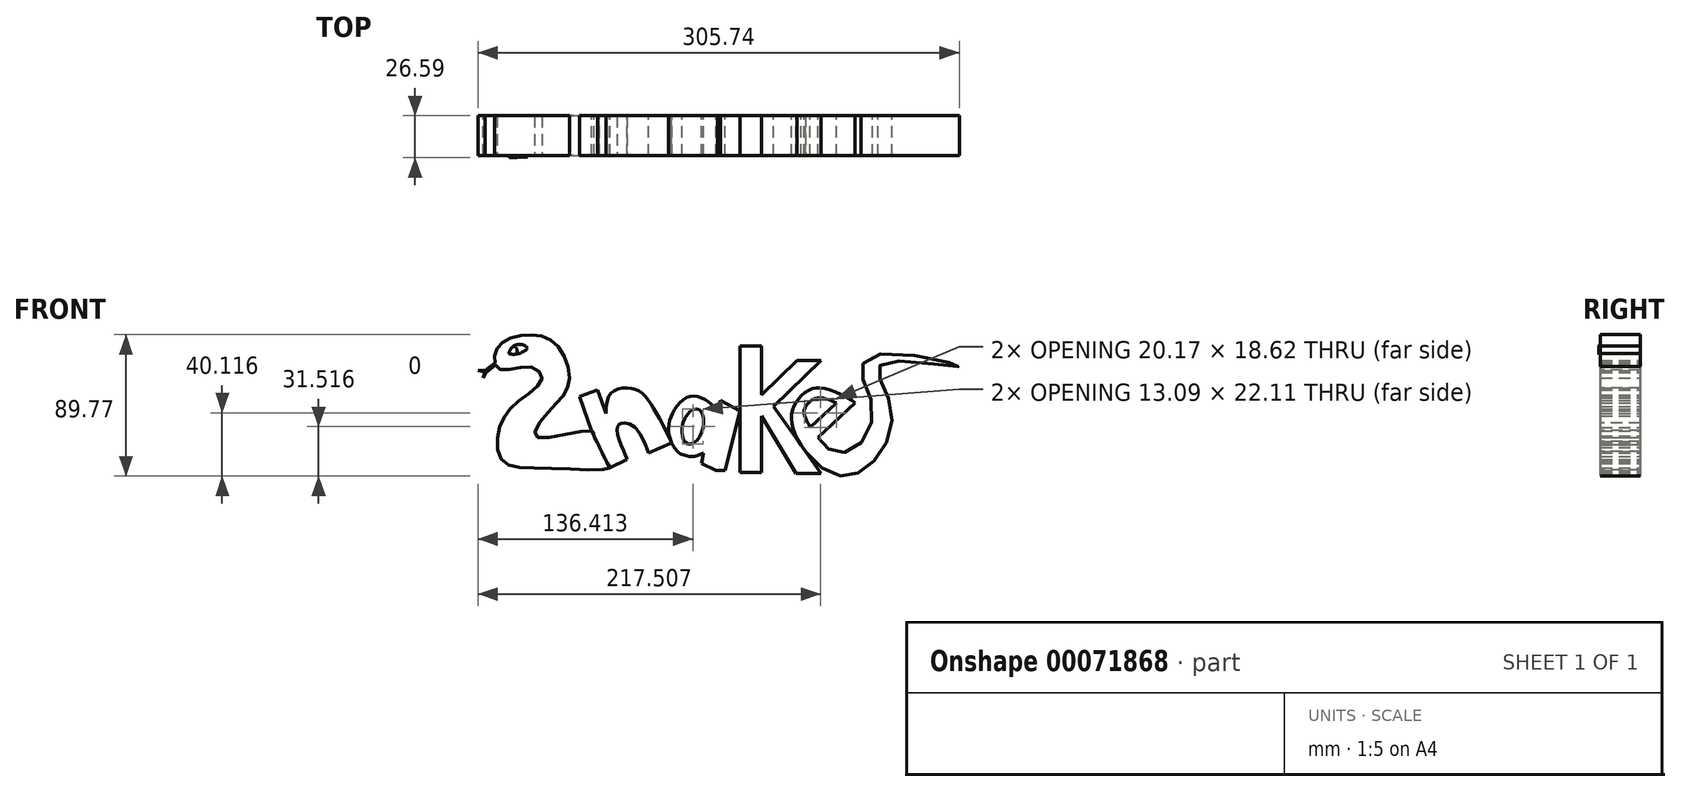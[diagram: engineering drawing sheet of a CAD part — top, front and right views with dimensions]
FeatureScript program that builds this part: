
annotation { "Feature Type Name" : "Feature", "Feature Type Description" : "" }
export const myFeature = defineFeature(function(context is Context, id is Id, definition is map)
    precondition{}
    {
        {
            var Q0;
            Q0=qCreatedBy(makeId("Front.planeOp"),FACE);
            var sketch = newSketch(context, id + "F0", { "sketchPlane" : qUnion([Q0])});
            skFitSpline(sketch, "E0", {"points": [v(-119.84, 21.1) * mm, v(-123.55, 27.84) * mm, v(-118.61, 38.3) * mm, v(-99.36, 43.22) * mm, v(-82.56, 35.03) * mm, v(-76.41, 12.09) * mm, v(-88.59, -4.8) * mm, v(-96.9, -21.5) * mm, v(-62.07, -17.82) * mm, v(-60.43, -21.12) * mm, v(-57.66, -26.68) * mm, v(-52.34, -37.36) * mm, v(-50.37, -41.31) * mm, v(-89.52, -41.59) * mm, v(-118.61, -36.67) * mm, v(-120.66, -16.6) * mm, v(-109.6, 0) * mm, v(-93.62, 14.95) * mm, v(-100.58, 22.74) * mm, v(-119.84, 21.1) * mm]});
            skLineSegment(sketch, "E1", {"start": v(-50.37, -41.31) * mm, "end": v(-62.07, -17.82) * mm});
            skLineSegment(sketch, "E2", {"start": v(-62.07, -17.82) * mm, "end": v(-69.7, 4.04) * mm});
            skLineSegment(sketch, "E3", {"start": v(-69.7, 4.04) * mm, "end": v(-58.05, 8.1) * mm});
            skLineSegment(sketch, "E4", {"start": v(-58.05, 8.1) * mm, "end": v(-52.9, -6.66) * mm});
            skFitSpline(sketch, "E5", {"points": [v(-52.9, -6.66) * mm, v(-49.31, 6.5) * mm, v(-35.25, 8.96) * mm, v(-24.7, 0) * mm, v(-11, -25.5) * mm], "startDerivative": vector(3.05, 68.8) * mm, "endDerivative": vector(42.91, -87.4) * mm});
            skLineSegment(sketch, "E6", {"start": v(-11, -25.5) * mm, "end": v(-25.76, -31.82) * mm});
            skFitSpline(sketch, "E7", {"points": [v(-25.76, -31.82) * mm, v(-32.79, -17.4) * mm, v(-40.17, -12.84) * mm, v(-45.8, -16) * mm, v(-39.47, -36.04) * mm, v(-39.82, -36.04) * mm], "startDerivative": vector(-23.2, 59.79) * mm, "endDerivative": vector(-11.8, 5.16) * mm});
            skLineSegment(sketch, "E8", {"start": v(-39.47, -36.04) * mm, "end": v(-50.37, -41.31) * mm});
            skLineSegment(sketch, "E9", {"start": v(-50.37, -41.31) * mm, "end": v(-50.37, -41.31) * mm});
            skLineSegment(sketch, "E10", {"start": v(7.83, -38.5) * mm, "end": v(17.12, -42.96) * mm});
            skLineSegment(sketch, "E11", {"start": v(17.12, -42.96) * mm, "end": v(22.69, -42.96) * mm});
            skLineSegment(sketch, "E12", {"start": v(22.69, -42.96) * mm, "end": v(32.34, -5.09) * mm});
            skLineSegment(sketch, "E13", {"start": v(32.34, -5.09) * mm, "end": v(20.08, 1.58) * mm});
            skLineSegment(sketch, "E14", {"start": v(20.08, 1.58) * mm, "end": v(18, -5) * mm});
            skLineSegment(sketch, "E15", {"start": v(7.83, -38.5) * mm, "end": v(9.16, -31.73) * mm});
            skFitSpline(sketch, "E16", {"points": [v(18, -5) * mm, v(11.8, 1.04) * mm, v(0.32, 4.05) * mm, v(-9.66, -5) * mm, v(-13.05, -16.28) * mm, v(-10.98, -25.69) * mm, v(-5.14, -32.46) * mm, v(4.08, -33.78) * mm, v(9.16, -31.73) * mm], "startDerivative": vector(-44.8, 53.4) * mm, "endDerivative": vector(47.88, 27.18) * mm});
            skEllipse(sketch, "E17", {"center": v(2.33, -14.96) * mm, "majorRadius": 11.45 * mm, "minorRadius": 6.5 * mm, "majorAxis": v(-0.26, -0.97)});
            skLineSegment(sketch, "E18", {"start": v(32.34, 36.08) * mm, "end": v(32.34, -44.27) * mm});
            skLineSegment(sketch, "E19", {"start": v(32.34, -44.27) * mm, "end": v(46.04, -44.27) * mm});
            skLineSegment(sketch, "E20", {"start": v(46.04, -44.27) * mm, "end": v(46.04, -8.22) * mm});
            skLineSegment(sketch, "E21", {"start": v(46.04, -8.22) * mm, "end": v(67.75, -44.67) * mm});
            skLineSegment(sketch, "E22", {"start": v(67.75, -44.67) * mm, "end": v(83.7, -44.67) * mm});
            skLineSegment(sketch, "E23", {"start": v(46.04, 5.07) * mm, "end": v(46.04, 36.08) * mm});
            skLineSegment(sketch, "E24", {"start": v(46.04, 36.08) * mm, "end": v(32.34, 36.08) * mm});
            skLineSegment(sketch, "E25", {"start": v(53.6, -2.23) * mm, "end": v(83.7, -44.67) * mm});
            skLineSegment(sketch, "E26", {"start": v(46.04, 5.07) * mm, "end": v(68.57, 26.83) * mm});
            skLineSegment(sketch, "E27", {"start": v(68.57, 26.83) * mm, "end": v(83.7, 26.83) * mm});
            skLineSegment(sketch, "E28", {"start": v(83.7, 26.83) * mm, "end": v(53.6, -2.23) * mm});
            skLineSegment(sketch, "E29", {"start": v(82, -21.92) * mm, "end": v(105.3, 0) * mm});
            skFitSpline(sketch, "E30", {"points": [v(105.3, 0) * mm, v(88.52, 8.55) * mm, v(77.48, 8.71) * mm, v(68.8, 1.6) * mm, v(65.03, -8.4) * mm, v(69.87, -24.91) * mm, v(90, -44.67) * mm, v(107.59, -44.16) * mm, v(124.35, -26.93) * mm, v(127.58, 0) * mm, v(119.85, 20.21) * mm, v(130, 26.5) * mm, v(171.65, 23.1) * mm, v(126.5, 31.4) * mm, v(109.22, 21.35) * mm, v(115.98, 0) * mm, v(108.58, -26.1) * mm, v(91.54, -30.93) * mm, v(82, -21.92) * mm], "startDerivative": vector(-184.22, 175.25) * mm, "endDerivative": vector(-182.9, 208.9) * mm});
            skFitSpline(sketch, "E31", {"points": [v(76.86, -15.67) * mm, v(73, -5.87) * mm, v(82, 3.14) * mm, v(93.51, 0) * mm], "startDerivative": vector(-2.6, 15.99) * mm, "endDerivative": vector(18.2, -6.44) * mm});
            skLineSegment(sketch, "E32", {"start": v(76.86, -15.67) * mm, "end": v(93.51, 0) * mm});
            skLineSegment(sketch, "E33", {"start": v(-123.28, 25.21) * mm, "end": v(-129.47, 20.44) * mm});
            skLineSegment(sketch, "E34", {"start": v(-129.47, 20.44) * mm, "end": v(-134.08, 20.44) * mm});
            skLineSegment(sketch, "E35", {"start": v(-134.08, 20.44) * mm, "end": v(-129.42, 19.73) * mm});
            skLineSegment(sketch, "E36", {"start": v(-129.42, 19.73) * mm, "end": v(-130.87, 15.73) * mm});
            skLineSegment(sketch, "E37", {"start": v(-130.87, 15.73) * mm, "end": v(-128.82, 19.34) * mm});
            skLineSegment(sketch, "E38", {"start": v(-128.82, 19.34) * mm, "end": v(-122.9, 24) * mm});
            skArc(sketch, "E39", {"start": v(-102.56, 34.75) * mm, "mid": v(-109.65, 36.91) * mm, "end": v(-114.43, 31.24) * mm});
            skArc(sketch, "E40", {"start": v(-114.43, 31.24) * mm, "mid": v(-108.01, 31.36) * mm, "end": v(-102.56, 34.75) * mm});
            skArc(sketch, "E41", {"start": v(-109.53, 31.02) * mm, "mid": v(-109.39, 33.96) * mm, "end": v(-111.4, 36.1) * mm});
            skArc(sketch, "E42", {"start": v(-112.92, 30.96) * mm, "mid": v(-112.57, 32.44) * mm, "end": v(-113.9, 33.16) * mm});
            skSolve(sketch);
        }
        {
            var Q0;
            {var subQ0=sQuery(id+"F0.wireOp",EDGE,"E33");Q0=makeQuery(id+"F0.imprint","IMPRINT",FACE,{"disambiguationData":[TD([[makeQuery(id+"F0.imprint","IMPRINT",EDGE,{"derivedFrom":subQ0}),1.0]])]});}
            var Q1;
            {var subQ0=sQuery(id+"F0.wireOp",EDGE,"E8");var subQ1=sQuery(id+"F0.wireOp",EDGE,"E7");var subQ2=makeQuery(id+"F0.imprint","INTERSECT",VERTEX,{"disambiguationData":[OD(0.0)],"derivedFrom":[subQ1,subQ0]});Q1=makeQuery(id+"F0.imprint","IMPRINT",FACE,{"disambiguationData":[TD([[makeQuery(id+"F0.imprint","IMPRINT",EDGE,{"disambiguationData":[TD([[subQ2,-1.0]])],"derivedFrom":subQ1}),-1.0]])]});}
            var Q2;
            {var subQ8=sQuery(id+"F0.wireOp",EDGE,"E19");Q2=makeQuery(id+"F0.imprint","IMPRINT",FACE,{"disambiguationData":[TD([[makeQuery(id+"F0.imprint","IMPRINT",EDGE,{"derivedFrom":subQ8}),1.0]])]});}
            var Q3;
            {var subQ0=sQuery(id+"F0.wireOp",EDGE,"E1");var subQ1=sQuery(id+"F0.wireOp",EDGE,"E0");var subQ3=makeQuery(id+"F0.imprint","INTERSECT",VERTEX,{"disambiguationData":[OD(0.0)],"derivedFrom":[subQ1,subQ0]});Q3=makeQuery(id+"F0.imprint","IMPRINT",FACE,{"disambiguationData":[TD([[makeQuery(id+"F0.imprint","IMPRINT",EDGE,{"disambiguationData":[TD([[subQ3,1.0]])],"derivedFrom":subQ1}),-1.0]])]});}
            var Q4;
            {var subQ0=sQuery(id+"F0.wireOp",EDGE,"E1");var subQ1=sQuery(id+"F0.wireOp",EDGE,"E0");var subQ3=makeQuery(id+"F0.imprint","INTERSECT",VERTEX,{"disambiguationData":[OD(3.0)],"derivedFrom":[subQ1,subQ0]});Q4=makeQuery(id+"F0.imprint","IMPRINT",FACE,{"disambiguationData":[TD([[makeQuery(id+"F0.imprint","IMPRINT",EDGE,{"disambiguationData":[TD([[subQ3,-1.0]])],"derivedFrom":subQ1}),-1.0]])]});}
            var Q5;
            Q5=makeQuery(id+"F0.imprint","IMPRINT",FACE,{"disambiguationData":[TD([[makeQuery(id+"F0.imprint","IMPRINT",EDGE,{"derivedFrom":sQuery(id+"F0.wireOp",EDGE,"E10")}),1.0]])]});
            var Q6;
            {var subQ0=sQuery(id+"F0.wireOp",EDGE,"E6");var subQ1=sQuery(id+"F0.wireOp",EDGE,"E5");var subQ2=makeQuery(id+"F0.imprint","INTERSECT",VERTEX,{"derivedFrom":[subQ1,subQ0]});Q6=makeQuery(id+"F0.imprint","IMPRINT",FACE,{"disambiguationData":[TD([[makeQuery(id+"F0.imprint","IMPRINT",EDGE,{"disambiguationData":[TD([[subQ2,1.0]])],"derivedFrom":subQ1}),-1.0]])]});}
            var Q7;
            {var subQ1=sQuery(id+"F0.wireOp",EDGE,"E29");Q7=makeQuery(id+"F0.imprint","IMPRINT",FACE,{"disambiguationData":[TD([[makeQuery(id+"F0.imprint","IMPRINT",EDGE,{"derivedFrom":subQ1}),1.0]])]});}
            var Q8;
            {var subQ0=sQuery(id+"F0.wireOp",EDGE,"E30");var subQ1=sQuery(id+"F0.wireOp",EDGE,"E25");var subQ2=makeQuery(id+"F0.imprint","INTERSECT",VERTEX,{"disambiguationData":[OD(0.0)],"derivedFrom":[subQ1,subQ0]});Q8=makeQuery(id+"F0.imprint","IMPRINT",FACE,{"disambiguationData":[TD([[makeQuery(id+"F0.imprint","IMPRINT",EDGE,{"disambiguationData":[TD([[subQ2,-1.0]])],"derivedFrom":subQ1}),-1.0]])]});}
            var Q9;
            {var subQ17=sQuery(id+"F0.wireOp",EDGE,"E2");Q9=makeQuery(id+"F0.imprint","IMPRINT",FACE,{"disambiguationData":[TD([[makeQuery(id+"F0.imprint","IMPRINT",EDGE,{"derivedFrom":subQ17}),-1.0]])]});}
            var Q10;
            {var subQ3=sQuery(id+"F0.wireOp",EDGE,"E41");Q10=makeQuery(id+"F0.imprint","IMPRINT",FACE,{"disambiguationData":[TD([[makeQuery(id+"F0.imprint","IMPRINT",EDGE,{"derivedFrom":subQ3}),-1.0]])]});}
            var Q11;
            {var subQ0=sQuery(id+"F0.wireOp",EDGE,"E41");Q11=makeQuery(id+"F0.imprint","IMPRINT",FACE,{"disambiguationData":[TD([[makeQuery(id+"F0.imprint","IMPRINT",EDGE,{"derivedFrom":subQ0}),1.0]])]});}
            var Q12;
            {var subQ3=sQuery(id+"F0.wireOp",EDGE,"E42");Q12=makeQuery(id+"F0.imprint","IMPRINT",FACE,{"disambiguationData":[TD([[makeQuery(id+"F0.imprint","IMPRINT",EDGE,{"derivedFrom":subQ3}),1.0]])]});}
            var Q13;
            {var subQ6=sQuery(id+"F0.wireOp",EDGE,"E0");var subQ8=makeQuery(id+"F0.imprint","INTERSECT",VERTEX,{"derivedFrom":[subQ6,sQuery(id+"F0.wireOp",EDGE,"E33")]});Q13=makeQuery(id+"F0.imprint","IMPRINT",FACE,{"disambiguationData":[TD([[makeQuery(id+"F0.imprint","IMPRINT",EDGE,{"disambiguationData":[TD([[subQ8,1.0]])],"derivedFrom":subQ6}),-1.0]])]});}
            extrude(context, id + "F1", {"entities" : qUnion([Q0, Q1, Q2, Q3, Q4, Q5, Q6, Q7, Q8, Q9, Q10, Q11, Q12, Q13]), "depth" : 25.4 * mm});
        }
        {
            var Q0;
            {var subQ0=sQuery(id+"F0.wireOp",EDGE,"E33");Q0=makeQuery(id+"F0.imprint","IMPRINT",FACE,{"disambiguationData":[TD([[makeQuery(id+"F0.imprint","IMPRINT",EDGE,{"derivedFrom":subQ0}),1.0]])]});}
            var Q1;
            {var subQ17=sQuery(id+"F0.wireOp",EDGE,"E2");Q1=makeQuery(id+"F0.imprint","IMPRINT",FACE,{"disambiguationData":[TD([[makeQuery(id+"F0.imprint","IMPRINT",EDGE,{"derivedFrom":subQ17}),-1.0]])]});}
            var Q2;
            Q2=makeQuery(id+"F0.imprint","IMPRINT",FACE,{"disambiguationData":[TD([[makeQuery(id+"F0.imprint","IMPRINT",EDGE,{"derivedFrom":sQuery(id+"F0.wireOp",EDGE,"E10")}),1.0]])]});
            var Q3;
            {var subQ8=sQuery(id+"F0.wireOp",EDGE,"E19");Q3=makeQuery(id+"F0.imprint","IMPRINT",FACE,{"disambiguationData":[TD([[makeQuery(id+"F0.imprint","IMPRINT",EDGE,{"derivedFrom":subQ8}),1.0]])]});}
            var Q4;
            {var subQ1=sQuery(id+"F0.wireOp",EDGE,"E29");Q4=makeQuery(id+"F0.imprint","IMPRINT",FACE,{"disambiguationData":[TD([[makeQuery(id+"F0.imprint","IMPRINT",EDGE,{"derivedFrom":subQ1}),1.0]])]});}
            var Q5;
            {var subQ6=sQuery(id+"F0.wireOp",EDGE,"E0");var subQ8=makeQuery(id+"F0.imprint","INTERSECT",VERTEX,{"derivedFrom":[subQ6,sQuery(id+"F0.wireOp",EDGE,"E33")]});Q5=makeQuery(id+"F0.imprint","IMPRINT",FACE,{"disambiguationData":[TD([[makeQuery(id+"F0.imprint","IMPRINT",EDGE,{"disambiguationData":[TD([[subQ8,1.0]])],"derivedFrom":subQ6}),-1.0]])]});}
            var Q6;
            {var subQ3=sQuery(id+"F0.wireOp",EDGE,"E41");Q6=makeQuery(id+"F0.imprint","IMPRINT",FACE,{"disambiguationData":[TD([[makeQuery(id+"F0.imprint","IMPRINT",EDGE,{"derivedFrom":subQ3}),-1.0]])]});}
            var Q7;
            {var subQ0=sQuery(id+"F0.wireOp",EDGE,"E41");Q7=makeQuery(id+"F0.imprint","IMPRINT",FACE,{"disambiguationData":[TD([[makeQuery(id+"F0.imprint","IMPRINT",EDGE,{"derivedFrom":subQ0}),1.0]])]});}
            var Q8;
            {var subQ3=sQuery(id+"F0.wireOp",EDGE,"E42");Q8=makeQuery(id+"F0.imprint","IMPRINT",FACE,{"disambiguationData":[TD([[makeQuery(id+"F0.imprint","IMPRINT",EDGE,{"derivedFrom":subQ3}),1.0]])]});}
            extrude(context, id + "F2", {"entities" : qUnion([Q0, Q1, Q2, Q3, Q4, Q5, Q6, Q7, Q8]), "depth" : 25.4 * mm});
        }
        {
            var Q0;
            {var subQ3=sQuery(id+"F0.wireOp",EDGE,"E41");Q0=makeQuery(id+"F0.imprint","IMPRINT",FACE,{"disambiguationData":[TD([[makeQuery(id+"F0.imprint","IMPRINT",EDGE,{"derivedFrom":subQ3}),-1.0]])]});}
            var Q1;
            {var subQ0=sQuery(id+"F0.wireOp",EDGE,"E41");Q1=makeQuery(id+"F0.imprint","IMPRINT",FACE,{"disambiguationData":[TD([[makeQuery(id+"F0.imprint","IMPRINT",EDGE,{"derivedFrom":subQ0}),1.0]])]});}
            var Q2;
            {var subQ3=sQuery(id+"F0.wireOp",EDGE,"E42");Q2=makeQuery(id+"F0.imprint","IMPRINT",FACE,{"disambiguationData":[TD([[makeQuery(id+"F0.imprint","IMPRINT",EDGE,{"derivedFrom":subQ3}),1.0]])]});}
            extrude(context, id + "F3", {"entities" : qUnion([Q0, Q1, Q2]), "operationType" : NewBodyOperationType.ADD, "depth" : 26.2 * mm});
        }
        {
            var Q0;
            {var subQ0=sQuery(id+"F0.wireOp",EDGE,"E41");Q0=makeQuery(id+"F0.imprint","IMPRINT",FACE,{"disambiguationData":[TD([[makeQuery(id+"F0.imprint","IMPRINT",EDGE,{"derivedFrom":subQ0}),1.0]])]});}
            var Q1;
            {var subQ3=sQuery(id+"F0.wireOp",EDGE,"E42");Q1=makeQuery(id+"F0.imprint","IMPRINT",FACE,{"disambiguationData":[TD([[makeQuery(id+"F0.imprint","IMPRINT",EDGE,{"derivedFrom":subQ3}),1.0]])]});}
            extrude(context, id + "F4", {"entities" : qUnion([Q0, Q1]), "operationType" : NewBodyOperationType.ADD, "depth" : 26.59 * mm});
        }
    });
